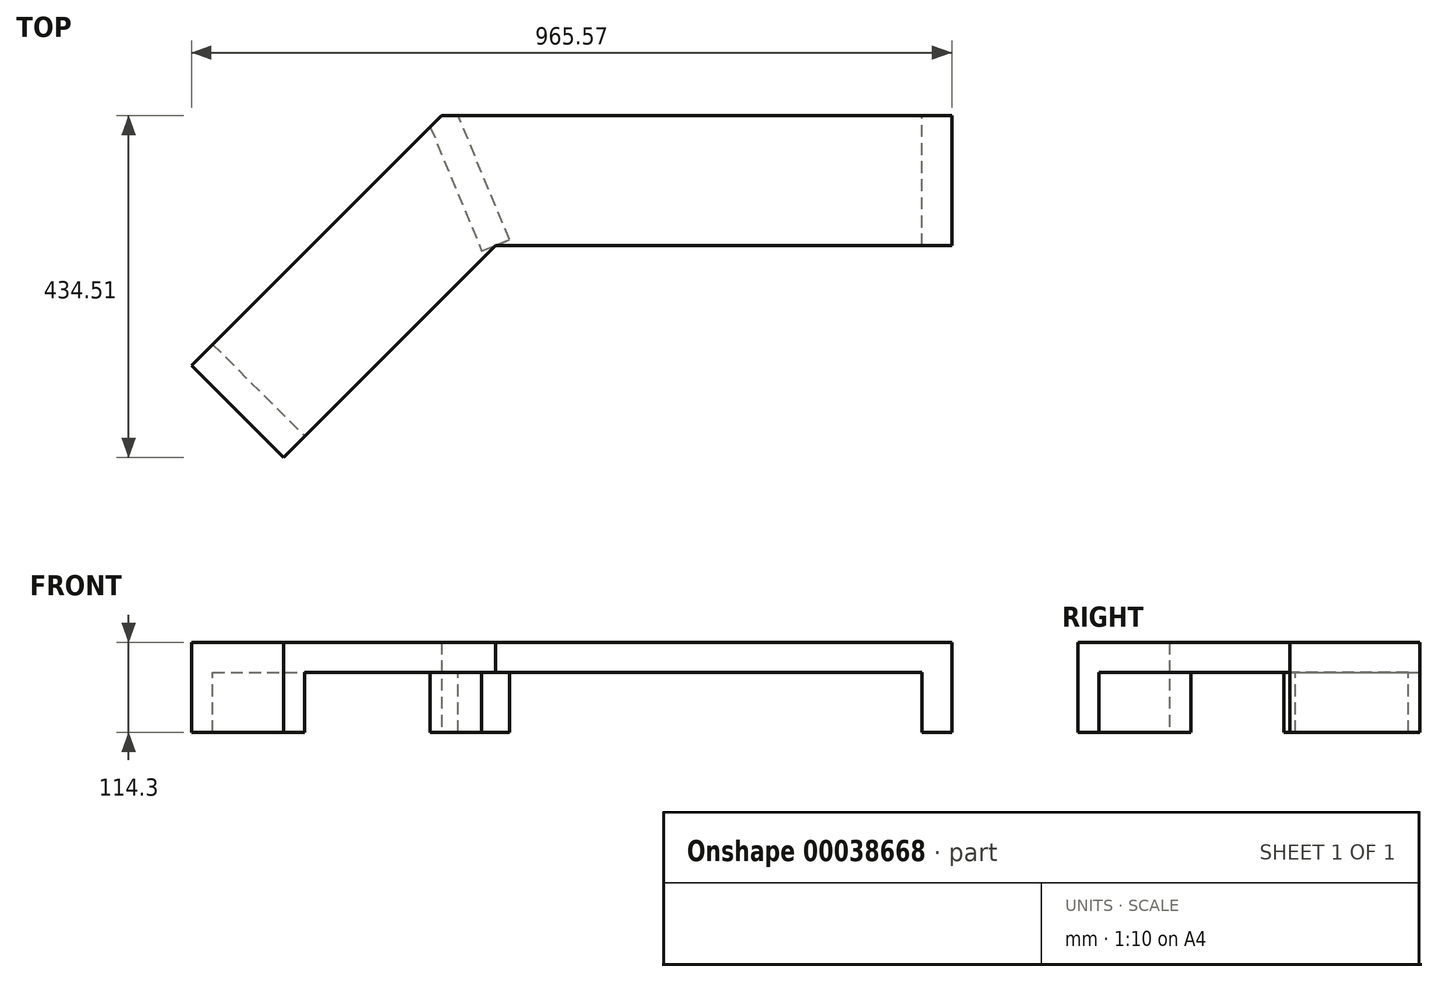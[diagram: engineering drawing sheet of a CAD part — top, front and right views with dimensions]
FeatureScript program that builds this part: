
annotation { "Feature Type Name" : "Feature", "Feature Type Description" : "" }
export const myFeature = defineFeature(function(context is Context, id is Id, definition is map)
    precondition{}
    {
        {
            var Q0;
            Q0=qCreatedBy(makeId("Top.planeOp"),FACE);
            var sketch = newSketch(context, id + "F0", { "sketchPlane" : qUnion([Q0])});
            skLineSegment(sketch, "E0", {"start": v(0, 82.55) * mm, "end": v(0, -82.55) * mm, "construction": true});
            skPoint(sketch, "E1", {"position": v(0, 0) * mm});
            skLineSegment(sketch, "E2", {"start": v(0, 82.55) * mm, "end": v(647.8, 82.55) * mm});
            skLineSegment(sketch, "E3", {"start": v(647.8, 82.55) * mm, "end": v(647.8, -82.55) * mm});
            skLineSegment(sketch, "E4", {"start": v(647.8, -82.55) * mm, "end": v(0, -82.55) * mm});
            skLineSegment(sketch, "E5", {"start": v(0, 82.55) * mm, "end": v(68.39, -82.55) * mm});
            skLineSegment(sketch, "E6", {"start": v(68.39, -82.55) * mm, "end": v(-201.02, -351.96) * mm});
            skLineSegment(sketch, "E7", {"start": v(-201.02, -351.96) * mm, "end": v(-317.76, -235.21) * mm});
            skLineSegment(sketch, "E8", {"start": v(-317.76, -235.21) * mm, "end": v(0, 82.55) * mm});
            skLineSegment(sketch, "E9", {"start": v(-14.58, 67.97) * mm, "end": v(53.8, -97.13) * mm, "construction": true});
            skLineSegment(sketch, "E10", {"start": v(89, -82.55) * mm, "end": v(20.62, 82.55) * mm, "construction": true});
            skLineSegment(sketch, "E11", {"start": v(19.61, -14.58) * mm, "end": v(54.81, 0) * mm, "construction": true});
            skPoint(sketch, "E12", {"position": v(37.21, -7.3) * mm});
            skSolve(sketch);
        }
        {
            var Q0;
            Q0 = qSketchRegion(id + "F0", true);
            extrude(context, id + "F1", {"entities" : qUnion([Q0]), "depth" : 38.1 * mm});
        }
        {
            var Q0;
            Q0=makeQuery(id+"F1.opExtrude","CAP_FACE",FACE,{"disambiguationData":[OSD([sQuery(id+"F0.wireOp",EDGE,"E2"),sQuery(id+"F0.wireOp",EDGE,"E3"),sQuery(id+"F0.wireOp",EDGE,"E4"),sQuery(id+"F0.wireOp",EDGE,"E6"),sQuery(id+"F0.wireOp",EDGE,"E7"),sQuery(id+"F0.wireOp",EDGE,"E8")])],"isStart":true});
            var sketch = newSketch(context, id + "F2", { "sketchPlane" : qUnion([Q0])});
            skLineSegment(sketch, "E13", {"start": v(-317.76, 235.21) * mm, "end": v(-290.82, 208.27) * mm});
            skLineSegment(sketch, "E14", {"start": v(-290.82, 208.27) * mm, "end": v(-174.08, 325.02) * mm});
            skLineSegment(sketch, "E15", {"start": v(-174.08, 325.02) * mm, "end": v(-201.02, 351.96) * mm});
            skLineSegment(sketch, "E16", {"start": v(-201.02, 351.96) * mm, "end": v(-317.76, 235.21) * mm});
            skLineSegment(sketch, "E17", {"start": v(85.99, 75.26) * mm, "end": v(20.62, -82.55) * mm});
            skLineSegment(sketch, "E18", {"start": v(20.62, -82.55) * mm, "end": v(0, -82.55) * mm});
            skLineSegment(sketch, "E19", {"start": v(0, -82.55) * mm, "end": v(-14.58, -67.97) * mm});
            skLineSegment(sketch, "E20", {"start": v(-14.58, -67.97) * mm, "end": v(50.79, 89.84) * mm});
            skLineSegment(sketch, "E21", {"start": v(647.8, 82.55) * mm, "end": v(609.7, 82.55) * mm});
            skLineSegment(sketch, "E22", {"start": v(609.7, 82.55) * mm, "end": v(609.7, -82.55) * mm});
            skLineSegment(sketch, "E23", {"start": v(609.7, -82.55) * mm, "end": v(647.8, -82.55) * mm});
            skLineSegment(sketch, "E24", {"start": v(647.8, -82.55) * mm, "end": v(647.8, 82.55) * mm});
            skLineSegment(sketch, "E25", {"start": v(50.79, 89.84) * mm, "end": v(85.99, 75.26) * mm});
            skPoint(sketch, "E26", {"position": v(68.39, 82.55) * mm});
            skSolve(sketch);
        }
        {
            var Q0;
            Q0 = qSketchRegion(id + "F2", true);
            extrude(context, id + "F3", {"entities" : qUnion([Q0]), "operationType" : NewBodyOperationType.ADD, "depth" : 76.2 * mm});
        }
    });
